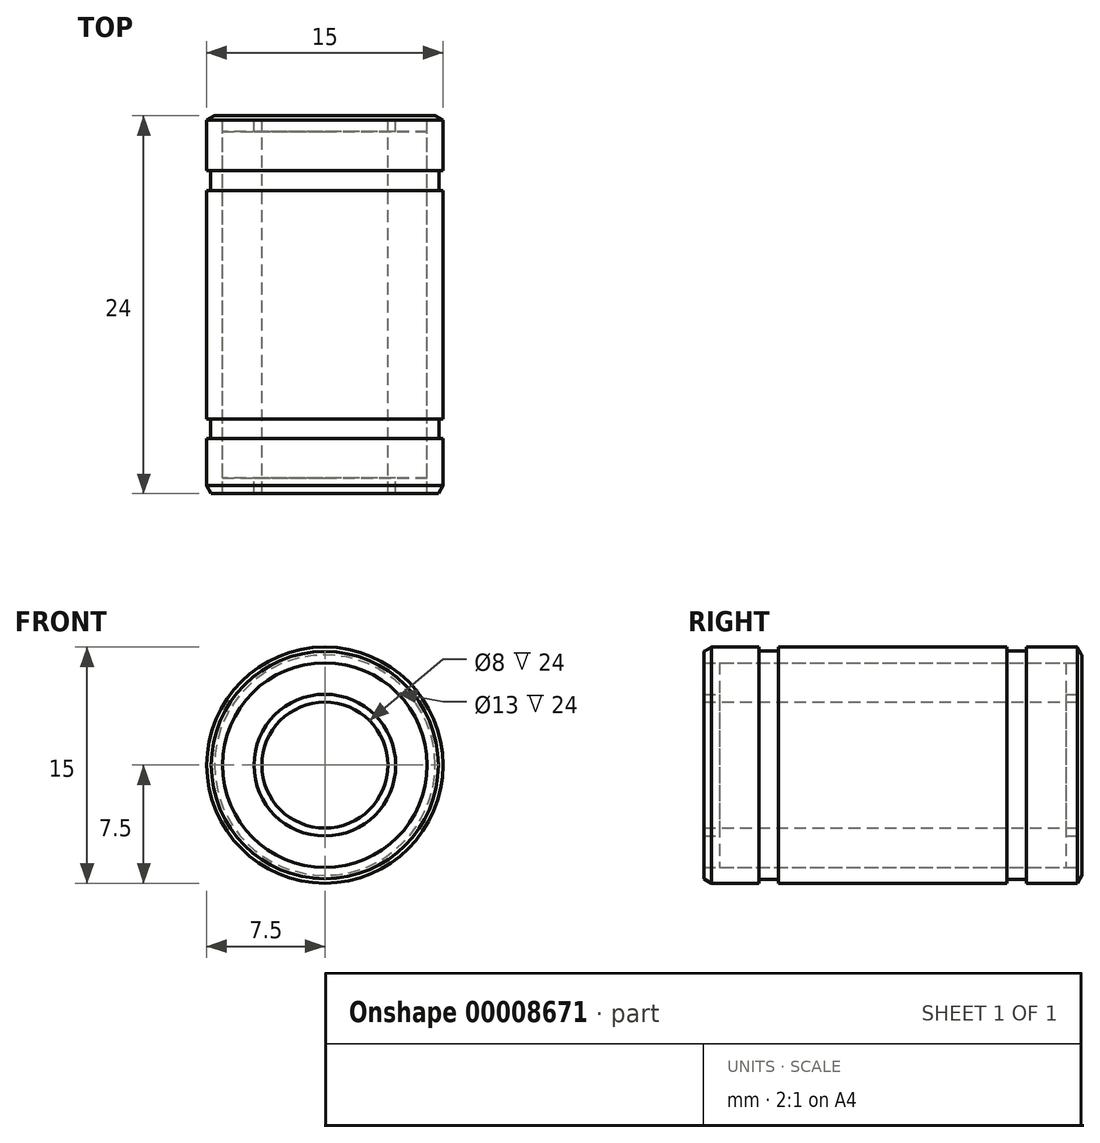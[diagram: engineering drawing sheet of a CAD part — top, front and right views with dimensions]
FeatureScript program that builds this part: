
annotation { "Feature Type Name" : "Feature", "Feature Type Description" : "" }
export const myFeature = defineFeature(function(context is Context, id is Id, definition is map)
    precondition{}
    {
        {
            var Q0;
            Q0=qCreatedBy(makeId("Top.planeOp"),FACE);
            var sketch = newSketch(context, id + "F0", { "sketchPlane" : qUnion([Q0])});
            skLineSegment(sketch, "E0.rect.bottom", {"start": v(7.5, -12) * mm, "end": v(-7.5, -12) * mm});
            skLineSegment(sketch, "E0.rect.top", {"start": v(7.5, 12) * mm, "end": v(-7.5, 12) * mm});
            skLineSegment(sketch, "E0.rect.left", {"start": v(7.5, -12) * mm, "end": v(7.5, 12) * mm});
            skLineSegment(sketch, "E0.rect.right", {"start": v(-7.5, -12) * mm, "end": v(-7.5, 12) * mm});
            skPoint(sketch, "E0.rect.middle", {"position": v(0, 0) * mm});
            skLineSegment(sketch, "E1.bottom", {"start": v(-7.5, -8.5) * mm, "end": v(7.5, -8.5) * mm});
            skLineSegment(sketch, "E1.top", {"start": v(-7.5, -7.25) * mm, "end": v(7.5, -7.25) * mm});
            skLineSegment(sketch, "E1.left", {"start": v(-7.5, -8.5) * mm, "end": v(-7.5, -7.25) * mm});
            skLineSegment(sketch, "E1.right", {"start": v(7.5, -8.5) * mm, "end": v(7.5, -7.25) * mm});
            skLineSegment(sketch, "E2.bottom", {"start": v(-7.5, 8.5) * mm, "end": v(7.5, 8.5) * mm});
            skLineSegment(sketch, "E2.top", {"start": v(-7.5, 7.25) * mm, "end": v(7.5, 7.25) * mm});
            skLineSegment(sketch, "E2.left", {"start": v(-7.5, 8.5) * mm, "end": v(-7.5, 7.25) * mm});
            skLineSegment(sketch, "E2.right", {"start": v(7.5, 8.5) * mm, "end": v(7.5, 7.25) * mm});
            skLineSegment(sketch, "E3", {"start": v(0, 12) * mm, "end": v(0, -12) * mm});
            skLineSegment(sketch, "E4.rect.right", {"start": v(-4, 12) * mm, "end": v(-4, -12) * mm});
            skLineSegment(sketch, "E5", {"start": v(-7.5, 11) * mm, "end": v(7.5, 11) * mm});
            skLineSegment(sketch, "E6", {"start": v(7.5, -11) * mm, "end": v(-7.5, -11) * mm});
            skLineSegment(sketch, "E7", {"start": v(-6.5, 12) * mm, "end": v(-6.5, -12) * mm});
            skLineSegment(sketch, "E8", {"start": v(-7.25, 8.5) * mm, "end": v(-7.25, 7.25) * mm});
            skLineSegment(sketch, "E9", {"start": v(-7.25, -7.25) * mm, "end": v(-7.25, -8.5) * mm});
            skLineSegment(sketch, "E10", {"start": v(-4.5, -12) * mm, "end": v(-4.5, -11) * mm});
            skLineSegment(sketch, "E11", {"start": v(-4.5, 11) * mm, "end": v(-4.5, 12) * mm});
            skSolve(sketch);
        }
        {
            var Q0;
            {var subQ3=sQuery(id+"F0.wireOp",EDGE,"E0.rect.top");var subQ5=sQuery(id+"F0.wireOp",EDGE,"E0.rect.right");var subQ7=makeQuery(id+"F0.imprint","INTERSECT",VERTEX,{"derivedFrom":[subQ3,subQ5]});Q0=makeQuery(id+"F0.imprint","IMPRINT",FACE,{"disambiguationData":[TD([[makeQuery(id+"F0.imprint","IMPRINT",EDGE,{"disambiguationData":[TD([[subQ7,1.0]])],"derivedFrom":subQ3}),1.0]])]});}
            var Q1;
            {var subQ3=sQuery(id+"F0.wireOp",EDGE,"E2.bottom");var subQ7=makeQuery(id+"F0.imprint","INTERSECT",VERTEX,{"derivedFrom":[subQ3,sQuery(id+"F0.wireOp",EDGE,"E8")]});Q1=makeQuery(id+"F0.imprint","IMPRINT",FACE,{"disambiguationData":[TD([[makeQuery(id+"F0.imprint","IMPRINT",EDGE,{"disambiguationData":[TD([[subQ7,-1.0]])],"derivedFrom":subQ3}),1.0]])]});}
            var Q2;
            {var subQ0=sQuery(id+"F0.wireOp",EDGE,"E8");Q2=makeQuery(id+"F0.imprint","IMPRINT",FACE,{"disambiguationData":[TD([[makeQuery(id+"F0.imprint","IMPRINT",EDGE,{"derivedFrom":subQ0}),1.0]])]});}
            var Q3;
            {var subQ3=sQuery(id+"F0.wireOp",EDGE,"E1.top");var subQ8=makeQuery(id+"F0.imprint","INTERSECT",VERTEX,{"derivedFrom":[subQ3,sQuery(id+"F0.wireOp",EDGE,"E9")]});Q3=makeQuery(id+"F0.imprint","IMPRINT",FACE,{"disambiguationData":[TD([[makeQuery(id+"F0.imprint","IMPRINT",EDGE,{"disambiguationData":[TD([[subQ8,-1.0]])],"derivedFrom":subQ3}),1.0]])]});}
            var Q4;
            {var subQ0=sQuery(id+"F0.wireOp",EDGE,"E9");Q4=makeQuery(id+"F0.imprint","IMPRINT",FACE,{"disambiguationData":[TD([[makeQuery(id+"F0.imprint","IMPRINT",EDGE,{"derivedFrom":subQ0}),1.0]])]});}
            var Q5;
            {var subQ3=sQuery(id+"F0.wireOp",EDGE,"E1.bottom");var subQ7=makeQuery(id+"F0.imprint","INTERSECT",VERTEX,{"derivedFrom":[subQ3,sQuery(id+"F0.wireOp",EDGE,"E9")]});Q5=makeQuery(id+"F0.imprint","IMPRINT",FACE,{"disambiguationData":[TD([[makeQuery(id+"F0.imprint","IMPRINT",EDGE,{"disambiguationData":[TD([[subQ7,-1.0]])],"derivedFrom":subQ3}),-1.0]])]});}
            var Q6;
            {var subQ3=sQuery(id+"F0.wireOp",EDGE,"E0.rect.bottom");var subQ5=sQuery(id+"F0.wireOp",EDGE,"E0.rect.right");var subQ7=makeQuery(id+"F0.imprint","INTERSECT",VERTEX,{"derivedFrom":[subQ3,subQ5]});Q6=makeQuery(id+"F0.imprint","IMPRINT",FACE,{"disambiguationData":[TD([[makeQuery(id+"F0.imprint","IMPRINT",EDGE,{"disambiguationData":[TD([[subQ7,1.0]])],"derivedFrom":subQ3}),-1.0]])]});}
            var Q7;
            Q7=sQuery(id+"F0.wireOp",EDGE,"E3");
            revolve(context, id + "F1", {"entities" : qUnion([Q0, Q1, Q2, Q3, Q4, Q5, Q6]), "axis" : qUnion([Q7]), "revolveType" : RevolveType.FULL});
        }
        {
            var Q0;
            {var subQ0=sQuery(id+"F0.wireOp",EDGE,"E10");Q0=makeQuery(id+"F0.imprint","IMPRINT",FACE,{"disambiguationData":[TD([[makeQuery(id+"F0.imprint","IMPRINT",EDGE,{"derivedFrom":subQ0}),-1.0]])]});}
            var Q1;
            {var subQ0=sQuery(id+"F0.wireOp",EDGE,"E7");var subQ3=sQuery(id+"F0.wireOp",EDGE,"E1.bottom");var subQ4=makeQuery(id+"F0.imprint","INTERSECT",VERTEX,{"derivedFrom":[subQ3,subQ0]});Q1=makeQuery(id+"F0.imprint","IMPRINT",FACE,{"disambiguationData":[TD([[makeQuery(id+"F0.imprint","IMPRINT",EDGE,{"disambiguationData":[TD([[subQ4,-1.0]])],"derivedFrom":subQ3}),-1.0]])]});}
            var Q2;
            {var subQ0=sQuery(id+"F0.wireOp",EDGE,"E7");var subQ3=sQuery(id+"F0.wireOp",EDGE,"E1.bottom");var subQ4=makeQuery(id+"F0.imprint","INTERSECT",VERTEX,{"derivedFrom":[subQ3,subQ0]});Q2=makeQuery(id+"F0.imprint","IMPRINT",FACE,{"disambiguationData":[TD([[makeQuery(id+"F0.imprint","IMPRINT",EDGE,{"disambiguationData":[TD([[subQ4,-1.0]])],"derivedFrom":subQ3}),1.0]])]});}
            var Q3;
            {var subQ0=sQuery(id+"F0.wireOp",EDGE,"E7");var subQ3=sQuery(id+"F0.wireOp",EDGE,"E1.top");var subQ4=makeQuery(id+"F0.imprint","INTERSECT",VERTEX,{"derivedFrom":[subQ3,subQ0]});Q3=makeQuery(id+"F0.imprint","IMPRINT",FACE,{"disambiguationData":[TD([[makeQuery(id+"F0.imprint","IMPRINT",EDGE,{"disambiguationData":[TD([[subQ4,-1.0]])],"derivedFrom":subQ3}),1.0]])]});}
            var Q4;
            {var subQ0=sQuery(id+"F0.wireOp",EDGE,"E7");var subQ3=sQuery(id+"F0.wireOp",EDGE,"E2.bottom");var subQ4=makeQuery(id+"F0.imprint","INTERSECT",VERTEX,{"derivedFrom":[subQ3,subQ0]});Q4=makeQuery(id+"F0.imprint","IMPRINT",FACE,{"disambiguationData":[TD([[makeQuery(id+"F0.imprint","IMPRINT",EDGE,{"disambiguationData":[TD([[subQ4,-1.0]])],"derivedFrom":subQ3}),-1.0]])]});}
            var Q5;
            {var subQ0=sQuery(id+"F0.wireOp",EDGE,"E7");var subQ3=sQuery(id+"F0.wireOp",EDGE,"E2.bottom");var subQ4=makeQuery(id+"F0.imprint","INTERSECT",VERTEX,{"derivedFrom":[subQ3,subQ0]});Q5=makeQuery(id+"F0.imprint","IMPRINT",FACE,{"disambiguationData":[TD([[makeQuery(id+"F0.imprint","IMPRINT",EDGE,{"disambiguationData":[TD([[subQ4,-1.0]])],"derivedFrom":subQ3}),1.0]])]});}
            var Q6;
            {var subQ0=sQuery(id+"F0.wireOp",EDGE,"E11");Q6=makeQuery(id+"F0.imprint","IMPRINT",FACE,{"disambiguationData":[TD([[makeQuery(id+"F0.imprint","IMPRINT",EDGE,{"derivedFrom":subQ0}),-1.0]])]});}
            var Q7;
            Q7=sQuery(id+"F0.wireOp",EDGE,"E3");
            revolve(context, id + "F2", {"entities" : qUnion([Q0, Q1, Q2, Q3, Q4, Q5, Q6]), "axis" : qUnion([Q7]), "revolveType" : RevolveType.FULL});
        }
        {
            var Q0;
            Q0=makeQuery(id+"F1.opRevolve","SWEPT_EDGE",EDGE,{"disambiguationData":[OSD([sQuery(id+"F0.wireOp",EDGE,"E0.rect.bottom"),sQuery(id+"F0.wireOp",EDGE,"E0.rect.right")])]});
            var Q1;
            Q1=makeQuery(id+"F1.opRevolve","SWEPT_EDGE",EDGE,{"disambiguationData":[OSD([sQuery(id+"F0.wireOp",EDGE,"E0.rect.top"),sQuery(id+"F0.wireOp",EDGE,"E0.rect.right")])]});
            chamfer(context, id + "F3", {"entities" : qUnion([Q0, Q1]), "chamferType" : ChamferType.OFFSET_ANGLE, "width" : .5 * mm, "oppositeDirection" : false, "angle" : 30 * degree, "tangentPropagation" : true});
        }
    });
